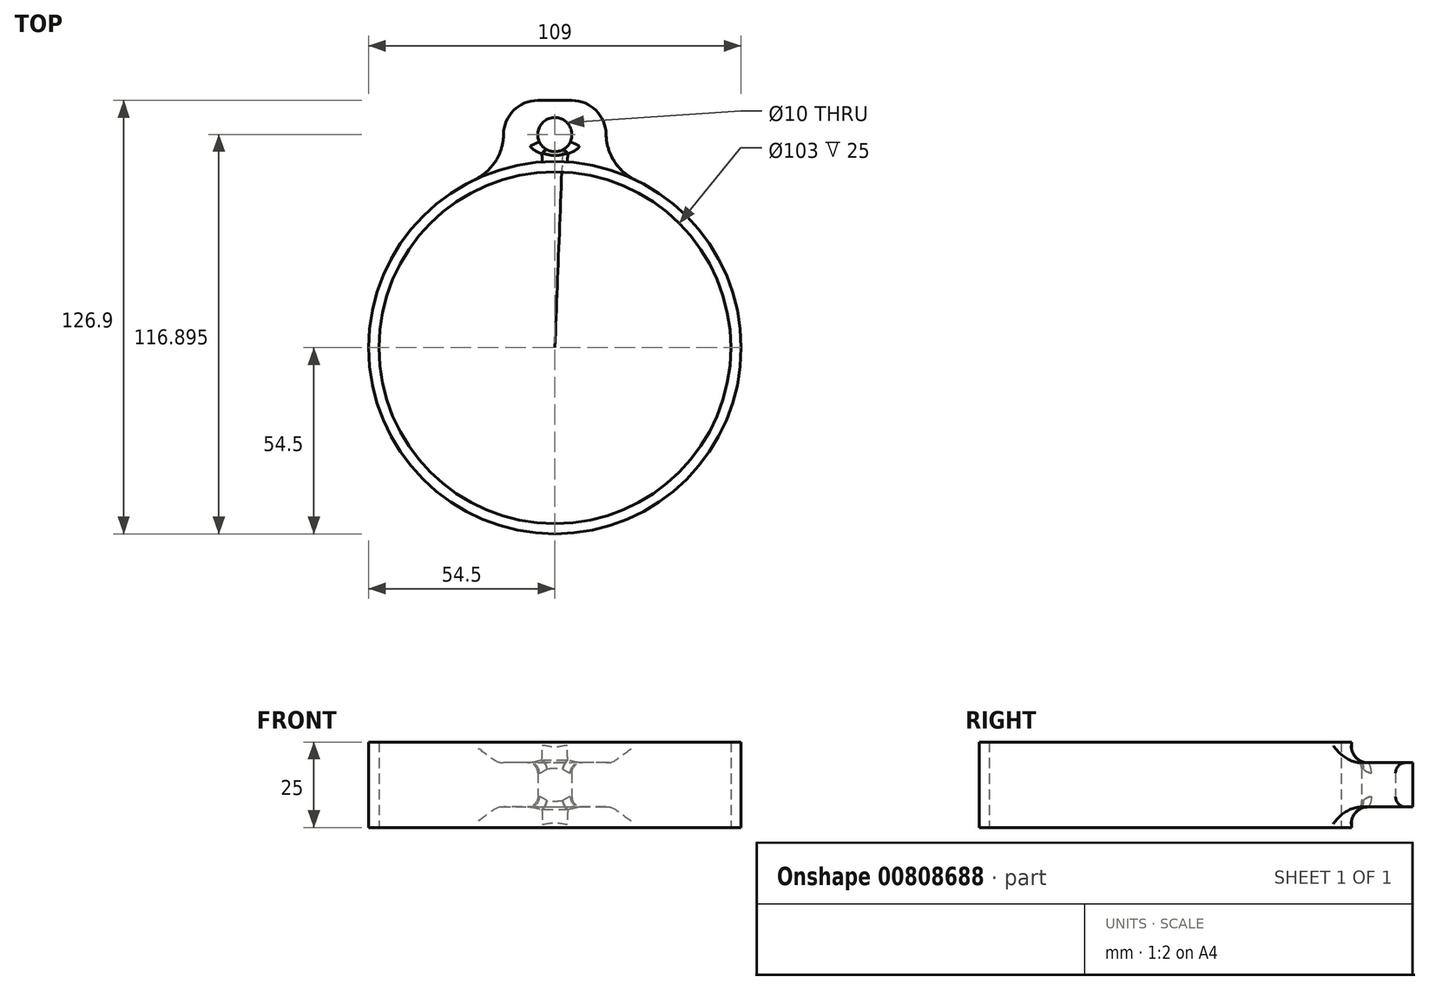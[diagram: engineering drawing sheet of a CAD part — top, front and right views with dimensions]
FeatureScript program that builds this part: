
annotation { "Feature Type Name" : "Feature", "Feature Type Description" : "" }
export const myFeature = defineFeature(function(context is Context, id is Id, definition is map)
    precondition{}
    {
        {
            var Q0;
            Q0=qCreatedBy(makeId("Top.planeOp"),FACE);
            var sketch = newSketch(context, id + "F0", { "sketchPlane" : qUnion([Q0])});
            skArc(sketch, "E0", {"start": v(-15, 52.4) * mm, "mid": v(0, -54.5) * mm, "end": v(15, 52.4) * mm});
            skCircle(sketch, "E1", {"center": v(0, 0) * mm, "radius": 51.5 * mm});
            skLineSegment(sketch, "E2", {"start": v(-15, 52.4) * mm, "end": v(-15, 72.4) * mm});
            skLineSegment(sketch, "E3", {"start": v(-15, 72.4) * mm, "end": v(15, 72.4) * mm});
            skLineSegment(sketch, "E4", {"start": v(15, 72.4) * mm, "end": v(15, 52.4) * mm});
            skLineSegment(sketch, "E5", {"start": v(0, 0) * mm, "end": v(0, 75.37) * mm, "construction": true});
            skCircle(sketch, "E6", {"center": v(0, 62.4) * mm, "radius": 5 * mm});
            skSolve(sketch);
        }
        {
            var Q0;
            Q0=makeQuery(id+"F0.imprint","IMPRINT",FACE,{"disambiguationData":[TD([[makeQuery(id+"F0.imprint","IMPRINT",EDGE,{"derivedFrom":sQuery(id+"F0.wireOp",EDGE,"E0")}),1.0]])]});
            extrude(context, id + "F1", {"entities" : qUnion([Q0]), "depth" : 25 * mm, "offsetDistance" : 25 * mm});
        }
        {
            var Q0;
            Q0=makeQuery(id+"F1.opExtrude","SWEPT_EDGE",EDGE,{"disambiguationData":[OSD([sQuery(id+"F0.wireOp",EDGE,"E0"),sQuery(id+"F0.wireOp",EDGE,"E2")])]});
            var Q1;
            Q1=makeQuery(id+"F1.opExtrude","SWEPT_EDGE",EDGE,{"disambiguationData":[OSD([sQuery(id+"F0.wireOp",EDGE,"E0"),sQuery(id+"F0.wireOp",EDGE,"E4")])]});
            fillet(context, id + "F2", {"entities" : qUnion([Q0, Q1]), "radius" : 15 * mm, "tangentPropagation" : true, "allowEdgeOverflow" : false});
        }
        {
            var Q0;
            Q0=makeQuery(id+"F1.opExtrude","SWEPT_EDGE",EDGE,{"disambiguationData":[OSD([sQuery(id+"F0.wireOp",EDGE,"E3"),sQuery(id+"F0.wireOp",EDGE,"E4")])]});
            var Q1;
            Q1=makeQuery(id+"F1.opExtrude","SWEPT_EDGE",EDGE,{"disambiguationData":[OSD([sQuery(id+"F0.wireOp",EDGE,"E2"),sQuery(id+"F0.wireOp",EDGE,"E3")])]});
            fillet(context, id + "F3", {"entities" : qUnion([Q0, Q1]), "radius" : 10 * mm, "tangentPropagation" : true, "allowEdgeOverflow" : false});
        }
        {
            var Q0;
            Q0=makeQuery(id+"F1.opExtrude","CAP_FACE",FACE,{"disambiguationData":[OSD([sQuery(id+"F0.wireOp",EDGE,"E0"),sQuery(id+"F0.wireOp",EDGE,"E1"),sQuery(id+"F0.wireOp",EDGE,"E2"),sQuery(id+"F0.wireOp",EDGE,"E3"),sQuery(id+"F0.wireOp",EDGE,"E4"),sQuery(id+"F0.wireOp",EDGE,"E6")])],"isStart":false});
            var sketch = newSketch(context, id + "F4", { "sketchPlane" : qUnion([Q0])});
            skArc(sketch, "E7.0", {"start": v(23.53, 49.16) * mm, "mid": v(17.36, 54.62) * mm, "end": v(15, 62.51) * mm});
            skArc(sketch, "E7.1", {"start": v(15, 62.51) * mm, "mid": v(12.03, 69.5) * mm, "end": v(5, 72.4) * mm});
            skLineSegment(sketch, "E7.2", {"start": v(-5, 72.4) * mm, "end": v(5, 72.4) * mm});
            skArc(sketch, "E7.3", {"start": v(-5, 72.4) * mm, "mid": v(-12.03, 69.5) * mm, "end": v(-15, 62.51) * mm});
            skArc(sketch, "E7.4", {"start": v(-15, 62.51) * mm, "mid": v(-17.36, 54.62) * mm, "end": v(-23.53, 49.16) * mm});
            skArc(sketch, "E8", {"start": v(-23.53, 49.16) * mm, "mid": v(0, 54.5) * mm, "end": v(23.53, 49.16) * mm});
            skSolve(sketch);
        }
        {
            var Q0;
            Q0=makeQuery(id+"F4.imprint","IMPRINT",FACE,{"disambiguationData":[TD([[makeQuery(id+"F4.imprint","IMPRINT",EDGE,{"derivedFrom":sQuery(id+"F4.wireOp",EDGE,"E7.0")}),1.0]])]});
            extrude(context, id + "F5", {"entities" : qUnion([Q0]), "operationType" : NewBodyOperationType.REMOVE, "oppositeDirection" : true, "depth" : 6 * mm, "offsetDistance" : 25 * mm});
        }
        {
            var Q0;
            Q0=makeQuery(id+"F1.opExtrude","CAP_FACE",FACE,{"disambiguationData":[OSD([sQuery(id+"F0.wireOp",EDGE,"E0"),sQuery(id+"F0.wireOp",EDGE,"E1"),sQuery(id+"F0.wireOp",EDGE,"E2"),sQuery(id+"F0.wireOp",EDGE,"E3"),sQuery(id+"F0.wireOp",EDGE,"E4"),sQuery(id+"F0.wireOp",EDGE,"E6")])],"isStart":true});
            var sketch = newSketch(context, id + "F6", { "sketchPlane" : qUnion([Q0])});
            skArc(sketch, "E9.0", {"start": v(15, -62.51) * mm, "mid": v(17.36, -54.62) * mm, "end": v(23.53, -49.16) * mm});
            skArc(sketch, "E9.1", {"start": v(5, -72.4) * mm, "mid": v(12.03, -69.5) * mm, "end": v(15, -62.51) * mm});
            skLineSegment(sketch, "E9.2", {"start": v(-5, -72.4) * mm, "end": v(5, -72.4) * mm});
            skArc(sketch, "E9.3", {"start": v(-15, -62.51) * mm, "mid": v(-12.03, -69.5) * mm, "end": v(-5, -72.4) * mm});
            skArc(sketch, "E9.4", {"start": v(-23.53, -49.16) * mm, "mid": v(-17.36, -54.62) * mm, "end": v(-15, -62.51) * mm});
            skArc(sketch, "E10", {"start": v(23.53, -49.16) * mm, "mid": v(0, -54.5) * mm, "end": v(-23.53, -49.16) * mm});
            skSolve(sketch);
        }
        {
            var Q0;
            Q0=makeQuery(id+"F6.imprint","IMPRINT",FACE,{"disambiguationData":[TD([[makeQuery(id+"F6.imprint","IMPRINT",EDGE,{"derivedFrom":sQuery(id+"F6.wireOp",EDGE,"E9.0")}),1.0]])]});
            extrude(context, id + "F7", {"entities" : qUnion([Q0]), "operationType" : NewBodyOperationType.REMOVE, "oppositeDirection" : true, "depth" : 6 * mm, "offsetDistance" : 25 * mm});
        }
        {
            var Q0;
            Q0=makeQuery(id+"F7.boolean.opBoolean","COPY",EDGE,{"derivedFrom":makeQuery(id+"F7.opExtrude","CAP_EDGE",EDGE,{"disambiguationData":[OSD([sQuery(id+"F6.wireOp",EDGE,"E10")])],"isStart":false})});
            var Q1;
            Q1=makeQuery(id+"F5.boolean.opBoolean","COPY",EDGE,{"derivedFrom":makeQuery(id+"F5.opExtrude","CAP_EDGE",EDGE,{"disambiguationData":[OSD([sQuery(id+"F4.wireOp",EDGE,"E8")])],"isStart":false})});
            fillet(context, id + "F8", {"entities" : qUnion([Q0, Q1]), "radius" : 5 * mm, "tangentPropagation" : true, "allowEdgeOverflow" : false});
        }
        {
            var Q0;
            Q0=makeQuery(id+"F7.boolean.opBoolean","COPY",EDGE,{"derivedFrom":makeQuery(id+"F7.opExtrude","CAP_EDGE",EDGE,{"disambiguationData":[OSD([sQuery(id+"F0.wireOp",EDGE,"E6")])],"isStart":false})});
            var Q1;
            Q1=makeQuery(id+"F8.opFillet","BLEND_EDGE",EDGE,{"blendedFrom":[makeQuery(id+"F7.boolean.opBoolean","COPY",EDGE,{"derivedFrom":makeQuery(id+"F7.opExtrude","CAP_EDGE",EDGE,{"disambiguationData":[OSD([sQuery(id+"F6.wireOp",EDGE,"E10")])],"isStart":false})}),makeQuery(id+"F1.opExtrude","SWEPT_FACE",FACE,{"disambiguationData":[OSD([sQuery(id+"F0.wireOp",EDGE,"E6")])]})],"blendedInto":[makeQuery(id+"F1.opExtrude","SWEPT_FACE",FACE,{"disambiguationData":[OSD([sQuery(id+"F0.wireOp",EDGE,"E6")])]})]});
            var Q2;
            Q2=makeQuery(id+"F5.boolean.opBoolean","COPY",EDGE,{"derivedFrom":makeQuery(id+"F5.opExtrude","CAP_EDGE",EDGE,{"disambiguationData":[OSD([sQuery(id+"F0.wireOp",EDGE,"E6")])],"isStart":false})});
            var Q3;
            Q3=makeQuery(id+"F8.opFillet","BLEND_EDGE",EDGE,{"blendedFrom":[makeQuery(id+"F5.boolean.opBoolean","COPY",EDGE,{"derivedFrom":makeQuery(id+"F5.opExtrude","CAP_EDGE",EDGE,{"disambiguationData":[OSD([sQuery(id+"F4.wireOp",EDGE,"E8")])],"isStart":false})}),makeQuery(id+"F1.opExtrude","SWEPT_FACE",FACE,{"disambiguationData":[OSD([sQuery(id+"F0.wireOp",EDGE,"E6")])]})],"blendedInto":[makeQuery(id+"F1.opExtrude","SWEPT_FACE",FACE,{"disambiguationData":[OSD([sQuery(id+"F0.wireOp",EDGE,"E6")])]})]});
            fillet(context, id + "F9", {"entities" : qUnion([Q0, Q1, Q2, Q3]), "radius" : 3 * mm, "tangentPropagation" : true, "allowEdgeOverflow" : false});
        }
    });
